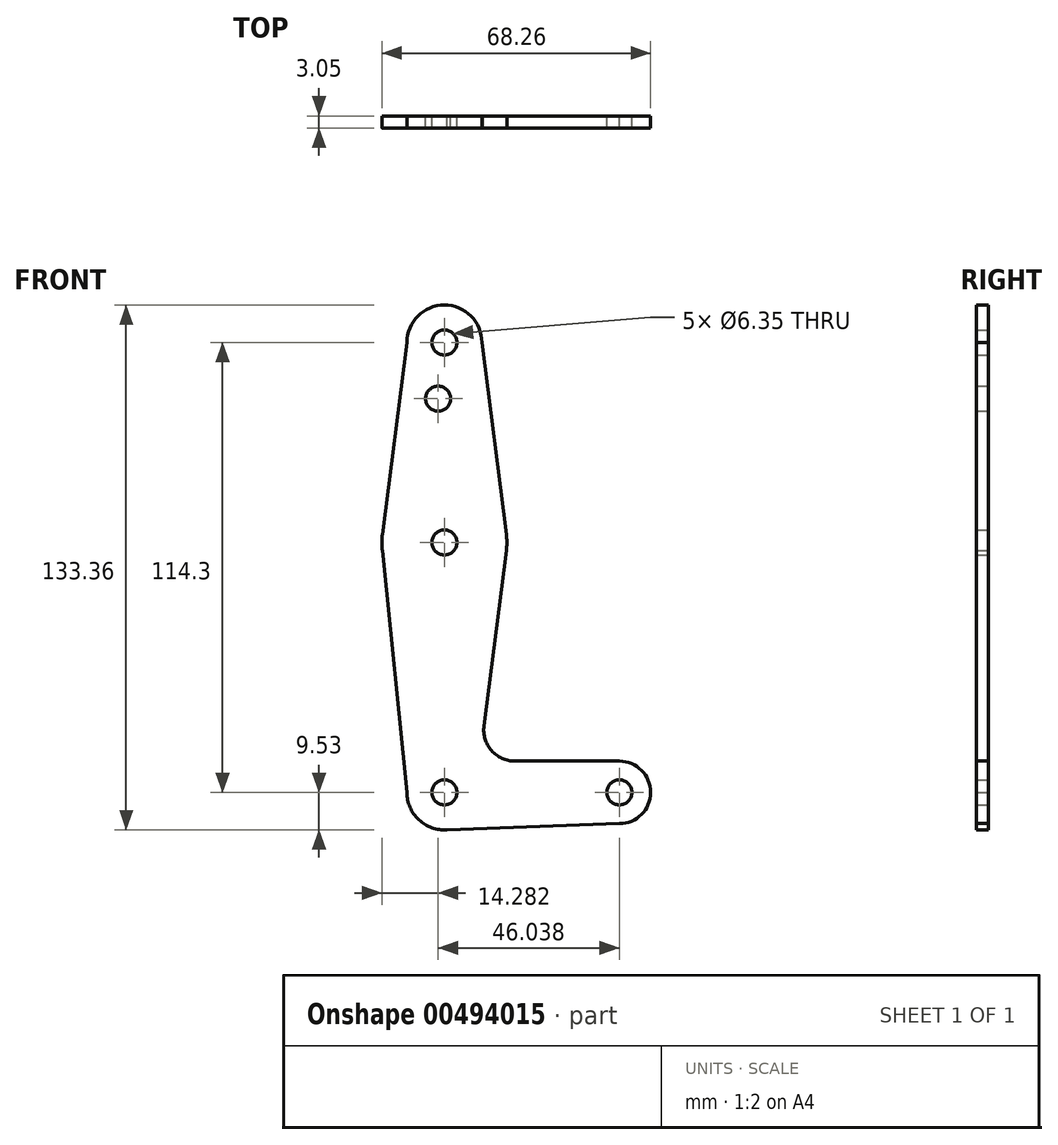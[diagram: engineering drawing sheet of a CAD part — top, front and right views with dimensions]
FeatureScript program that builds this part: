
annotation { "Feature Type Name" : "Feature", "Feature Type Description" : "" }
export const myFeature = defineFeature(function(context is Context, id is Id, definition is map)
    precondition{}
    {
        {
            var Q0;
            Q0=qCreatedBy(makeId("Front.planeOp"),FACE);
            var sketch = newSketch(context, id + "F0", { "sketchPlane" : qUnion([Q0])});
            skLineSegment(sketch, "E0", {"start": v(0, 0) * mm, "end": v(0, 114.3) * mm, "construction": true});
            skCircle(sketch, "E1", {"center": v(0, 0) * mm, "radius": 9.53 * mm});
            skCircle(sketch, "E2", {"center": v(0, 63.5) * mm, "radius": 15.88 * mm});
            skCircle(sketch, "E3", {"center": v(0, 114.3) * mm, "radius": 9.53 * mm});
            skLineSegment(sketch, "E4", {"start": v(0, 0) * mm, "end": v(44.45, 0) * mm, "construction": true});
            skCircle(sketch, "E5", {"center": v(44.45, 0) * mm, "radius": 7.94 * mm});
            skLineSegment(sketch, "E6", {"start": v(17.95, 7.94) * mm, "end": v(44.45, 7.94) * mm});
            skLineSegment(sketch, "E7", {"start": v(0, -9.52) * mm, "end": v(44.45, -7.94) * mm});
            skLineSegment(sketch, "E8", {"start": v(9.53, 114.3) * mm, "end": v(15.75, 65.5) * mm});
            skLineSegment(sketch, "E9", {"start": v(-15.75, 65.5) * mm, "end": v(-9.53, 114.3) * mm});
            skLineSegment(sketch, "E10", {"start": v(15.75, 61.5) * mm, "end": v(10.06, 16.9) * mm});
            skLineSegment(sketch, "E11", {"start": v(-15.75, 61.5) * mm, "end": v(-9.53, 0) * mm});
            skCircle(sketch, "E12", {"center": v(0, 114.3) * mm, "radius": 3.18 * mm});
            skCircle(sketch, "E13", {"center": v(0, 63.5) * mm, "radius": 3.18 * mm});
            skCircle(sketch, "E14", {"center": v(0, 0) * mm, "radius": 3.18 * mm});
            skCircle(sketch, "E15", {"center": v(44.45, 0) * mm, "radius": 3.18 * mm});
            skCircle(sketch, "E16", {"center": v(-1.59, 100.03) * mm, "radius": 3.18 * mm});
            skArc(sketch, "E17.filletArc", {"start": v(10.06, 16.9) * mm, "mid": v(11.98, 10.63) * mm, "end": v(17.95, 7.94) * mm});
            skSolve(sketch);
        }
        {
            var Q0;
            Q0 = qSketchRegion(id + "F0", true);
            var Q1;
            {var subQ1=sQuery(id+"F0.wireOp",EDGE,"E8");Q1=makeQuery(id+"F0.imprint","IMPRINT",FACE,{"disambiguationData":[TD([[makeQuery(id+"F0.imprint","IMPRINT",EDGE,{"derivedFrom":subQ1}),-1.0]])]});}
            extrude(context, id + "F1", {"entities" : qUnion([Q0, Q1]), "depth" : 3.05 * mm});
        }
    });
